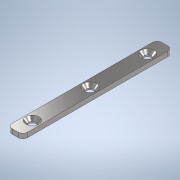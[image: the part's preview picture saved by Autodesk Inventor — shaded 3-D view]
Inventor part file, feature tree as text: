
AUTODESK INVENTOR PART (.ipt)
format: ipt  version: 2022 (Build 260153000, 153)  size: 122,368 bytes
history: native  units: in
note: dims shown in document units (in); Inventor stores cm internally (conversion verified against a paired STEP export)
features: sketch x2, extrude x1, hole x1, fillet x1
ambient origin geometry x8: Origin, YZ Plane, XZ Plane, XY Plane, X Axis, Y Axis, Z Axis, Center Point
bodies: Solid1 (feature_tree)
feature tree (5):
  extrude  "Extrusion1"  Depth=1.95in
  hole  "Hole1"  [1 undecoded]
  fillet  "Fillet1"  Radius=0.75in
  sketch  "Sketch1"  dims[d0=0.2in d1=1.95in]
  sketch  "Sketch2"  dims[d2=0.0625in d3=0.0in d4=0.75in d5=0.75in d6=0.096in d7=0.172in d8=0.172in d9=0.25in d10=0.5635in d11=1.0in d12=0.8108in d13=0.0625in]
note: 1 required parameter value undecoded (feature->parameter linkage not recoverable at this tier; creation-order binding heuristic only, values carry confidence <= 0.55)
